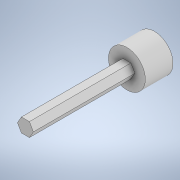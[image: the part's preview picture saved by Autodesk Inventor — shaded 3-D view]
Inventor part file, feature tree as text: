
AUTODESK INVENTOR PART (.ipt)
format: ipt  version: 2021.2 (Build 252289000, 289)  size: 113,152 bytes
history: native  units: in
note: dims shown in document units (in); Inventor stores cm internally (conversion verified against a paired STEP export)
features: extrude x2, sketch x2
ambient origin geometry x8: Origin, YZ Plane, XZ Plane, XY Plane, X Axis, Y Axis, Z Axis, Center Point
bodies: Body1 (feature_tree)
feature tree (4):
  extrude  "Extrusion2"  Depth=3.5in TaperAngle=0.0deg
  extrude  "Extrusion4"  Depth=1.0in
  sketch  "Sketch1"  dims[d0=0.375in d4=3.5in d5=0.0in]
  sketch  "Sketch4"  dims[d6=0.001in d10=1.0in d11=0.75in d12=0.0in]
